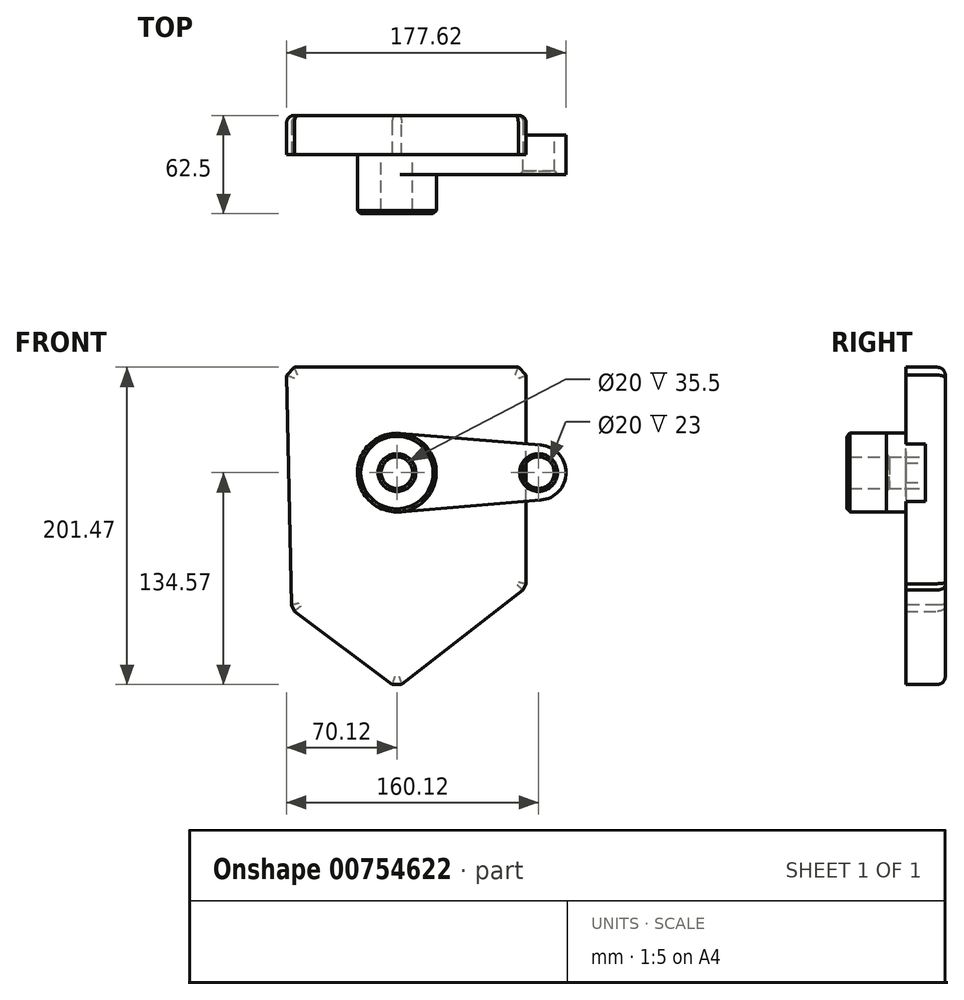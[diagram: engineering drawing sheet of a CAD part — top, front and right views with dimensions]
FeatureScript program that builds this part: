
annotation { "Feature Type Name" : "Feature", "Feature Type Description" : "" }
export const myFeature = defineFeature(function(context is Context, id is Id, definition is map)
    precondition{}
    {
        {
            var Q0;
            Q0=qCreatedBy(makeId("Front.planeOp"),FACE);
            var sketch = newSketch(context, id + "F0", { "sketchPlane" : qUnion([Q0])});
            skCircle(sketch, "E0", {"center": v(0, 0) * mm, "radius": 25 * mm});
            skCircle(sketch, "E1", {"center": v(90, 0) * mm, "radius": 17.5 * mm});
            skLineSegment(sketch, "E2", {"start": v(2.08, 24.91) * mm, "end": v(91.46, 17.44) * mm});
            skLineSegment(sketch, "E3", {"start": v(2.08, -24.91) * mm, "end": v(91.46, -17.44) * mm});
            skCircle(sketch, "E4", {"center": v(0, 0) * mm, "radius": 10 * mm});
            skCircle(sketch, "E5", {"center": v(90, 0) * mm, "radius": 10 * mm});
            skSolve(sketch);
        }
        {
            var Q0;
            Q0=qSketchRegion(id+"F0",true);
            extrude(context, id + "F1", {"entities" : qUnion([Q0]), "depth" : 25 * mm});
        }
        {
            var Q0;
            Q0=makeQuery(id+"F0.imprint","IMPRINT",FACE,{"disambiguationData":[TD([[makeQuery(id+"F0.imprint","IMPRINT",EDGE,{"derivedFrom":sQuery(id+"F0.wireOp",EDGE,"E4")}),-1.0]])]});
            extrude(context, id + "F2", {"entities" : qUnion([Q0]), "operationType" : NewBodyOperationType.ADD, "depth" : 50 * mm});
        }
        {
            var Q0;
            Q0=makeQuery(id+"F2.opExtrude","CAP_EDGE",EDGE,{"disambiguationData":[OSD([sQuery(id+"F0.wireOp",EDGE,"E0")])],"isStart":false});
            var Q1;
            Q1=makeQuery(id+"F2.opExtrude","CAP_EDGE",EDGE,{"disambiguationData":[OSD([sQuery(id+"F0.wireOp",EDGE,"E4")])],"isStart":false});
            var Q2;
            Q2=makeQuery(id+"F1.opExtrude","CAP_EDGE",EDGE,{"disambiguationData":[OSD([sQuery(id+"F0.wireOp",EDGE,"E5")])],"isStart":false});
            chamfer(context, id + "F3", {"entities" : qUnion([Q0, Q1, Q2]), "width" : 2 * mm, "tangentPropagation" : true});
        }
        {
            var Q0;
            Q0=qCreatedBy(makeId("Front.planeOp"),FACE);
            var sketch = newSketch(context, id + "F4", { "sketchPlane" : qUnion([Q0])});
            skLineSegment(sketch, "E6", {"start": v(-70.23, 66.9) * mm, "end": v(82.14, 66.9) * mm});
            skLineSegment(sketch, "E7", {"start": v(82.14, 66.9) * mm, "end": v(82.14, -73.03) * mm});
            skLineSegment(sketch, "E8", {"start": v(82.14, -73.03) * mm, "end": v(0, -136.86) * mm});
            skLineSegment(sketch, "E9", {"start": v(0, -136.86) * mm, "end": v(-66.92, -86.65) * mm});
            skLineSegment(sketch, "E10", {"start": v(-66.92, -86.65) * mm, "end": v(-70.23, 66.9) * mm});
            skSolve(sketch);
        }
        {
            var Q0;
            Q0 = qSketchRegion(id + "F4", true);
            extrude(context, id + "F5", {"entities" : qUnion([Q0]), "operationType" : NewBodyOperationType.ADD, "endBound" : BoundingType.SYMMETRIC, "depth" : 25 * mm, "offsetDistance" : 25 * mm});
        }
        {
            var Q0;
            Q0=makeQuery(id+"F5.opExtrude","SWEPT_EDGE",EDGE,{"disambiguationData":[OSD([sQuery(id+"F4.wireOp",EDGE,"E8"),sQuery(id+"F4.wireOp",EDGE,"E9")])]});
            var Q1;
            Q1=makeQuery(id+"F5.opExtrude","SWEPT_EDGE",EDGE,{"disambiguationData":[OSD([sQuery(id+"F4.wireOp",EDGE,"E9"),sQuery(id+"F4.wireOp",EDGE,"E10")])]});
            var Q2;
            Q2=makeQuery(id+"F5.opExtrude","SWEPT_EDGE",EDGE,{"disambiguationData":[OSD([sQuery(id+"F4.wireOp",EDGE,"E6"),sQuery(id+"F4.wireOp",EDGE,"E10")])]});
            var Q3;
            Q3=makeQuery(id+"F5.opExtrude","SWEPT_EDGE",EDGE,{"disambiguationData":[OSD([sQuery(id+"F4.wireOp",EDGE,"E7"),sQuery(id+"F4.wireOp",EDGE,"E8")])]});
            var Q4;
            Q4=makeQuery(id+"F5.opExtrude","SWEPT_EDGE",EDGE,{"disambiguationData":[OSD([sQuery(id+"F4.wireOp",EDGE,"E6"),sQuery(id+"F4.wireOp",EDGE,"E7")])]});
            chamfer(context, id + "F6", {"entities" : qUnion([Q0, Q1, Q2, Q3, Q4]), "width" : 5 * mm, "tangentPropagation" : true});
        }
        {
            var Q0;
            Q0=makeQuery(id+"F5.opExtrude","CAP_FACE",FACE,{"disambiguationData":[OSD([sQuery(id+"F4.wireOp",EDGE,"E6"),sQuery(id+"F4.wireOp",EDGE,"E7"),sQuery(id+"F4.wireOp",EDGE,"E8"),sQuery(id+"F4.wireOp",EDGE,"E9"),sQuery(id+"F4.wireOp",EDGE,"E10")])],"isStart":true});
            fillet(context, id + "F7", {"entities" : qUnion([Q0]), "radius" : 5 * mm, "tangentPropagation" : true, "allowEdgeOverflow" : false});
        }
    });
